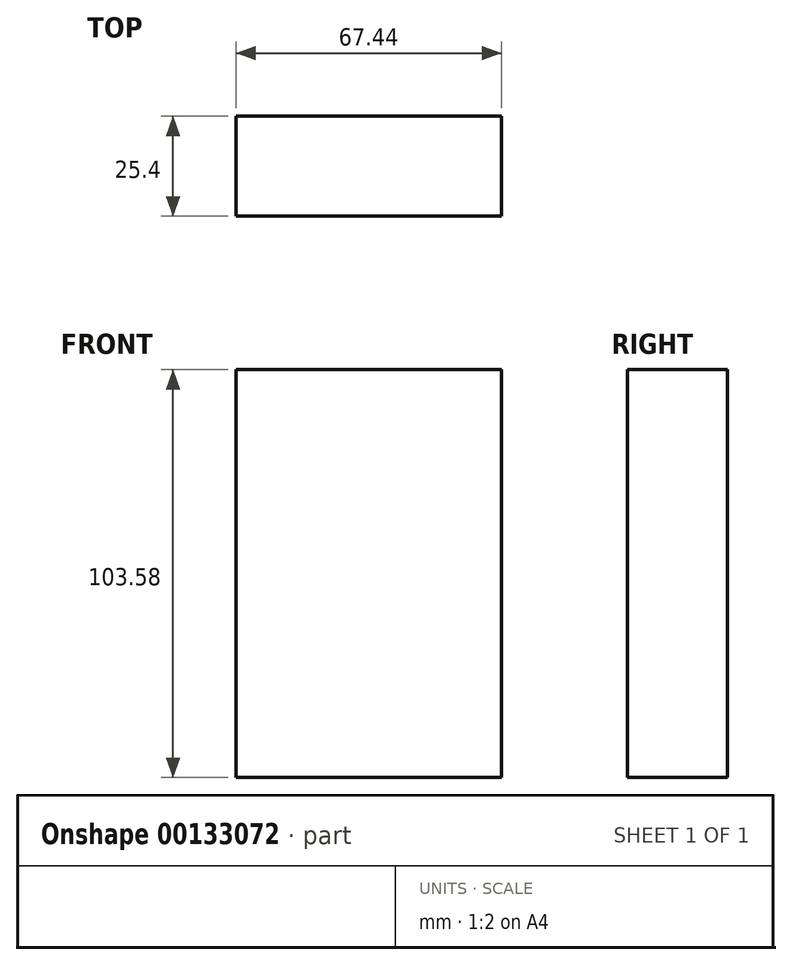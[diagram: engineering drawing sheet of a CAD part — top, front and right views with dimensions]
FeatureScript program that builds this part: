
annotation { "Feature Type Name" : "Feature", "Feature Type Description" : "" }
export const myFeature = defineFeature(function(context is Context, id is Id, definition is map)
    precondition{}
    {
        {
            var Q0;
            Q0=qCreatedBy(makeId("Front.planeOp"),FACE);
            var sketch = newSketch(context, id + "F0", { "sketchPlane" : qUnion([Q0])});
            skLineSegment(sketch, "E0.bottom", {"start": v(-76.1, -33.89) * mm, "end": v(-8.66, -33.89) * mm});
            skLineSegment(sketch, "E0.top", {"start": v(-76.1, 69.69) * mm, "end": v(-8.66, 69.69) * mm});
            skLineSegment(sketch, "E0.left", {"start": v(-76.1, -33.89) * mm, "end": v(-76.1, 69.69) * mm});
            skLineSegment(sketch, "E0.right", {"start": v(-8.66, -33.89) * mm, "end": v(-8.66, 69.69) * mm});
            skSolve(sketch);
        }
        {
            var Q0;
            Q0=makeQuery(id+"F0.imprint","IMPRINT",FACE,{"disambiguationData":[TD([[makeQuery(id+"F0.imprint","IMPRINT",EDGE,{"derivedFrom":sQuery(id+"F0.wireOp",EDGE,"E0.bottom")}),1.0]])]});
            extrude(context, id + "F1", {"entities" : qUnion([Q0]), "depth" : 25.4 * mm});
        }
    });
